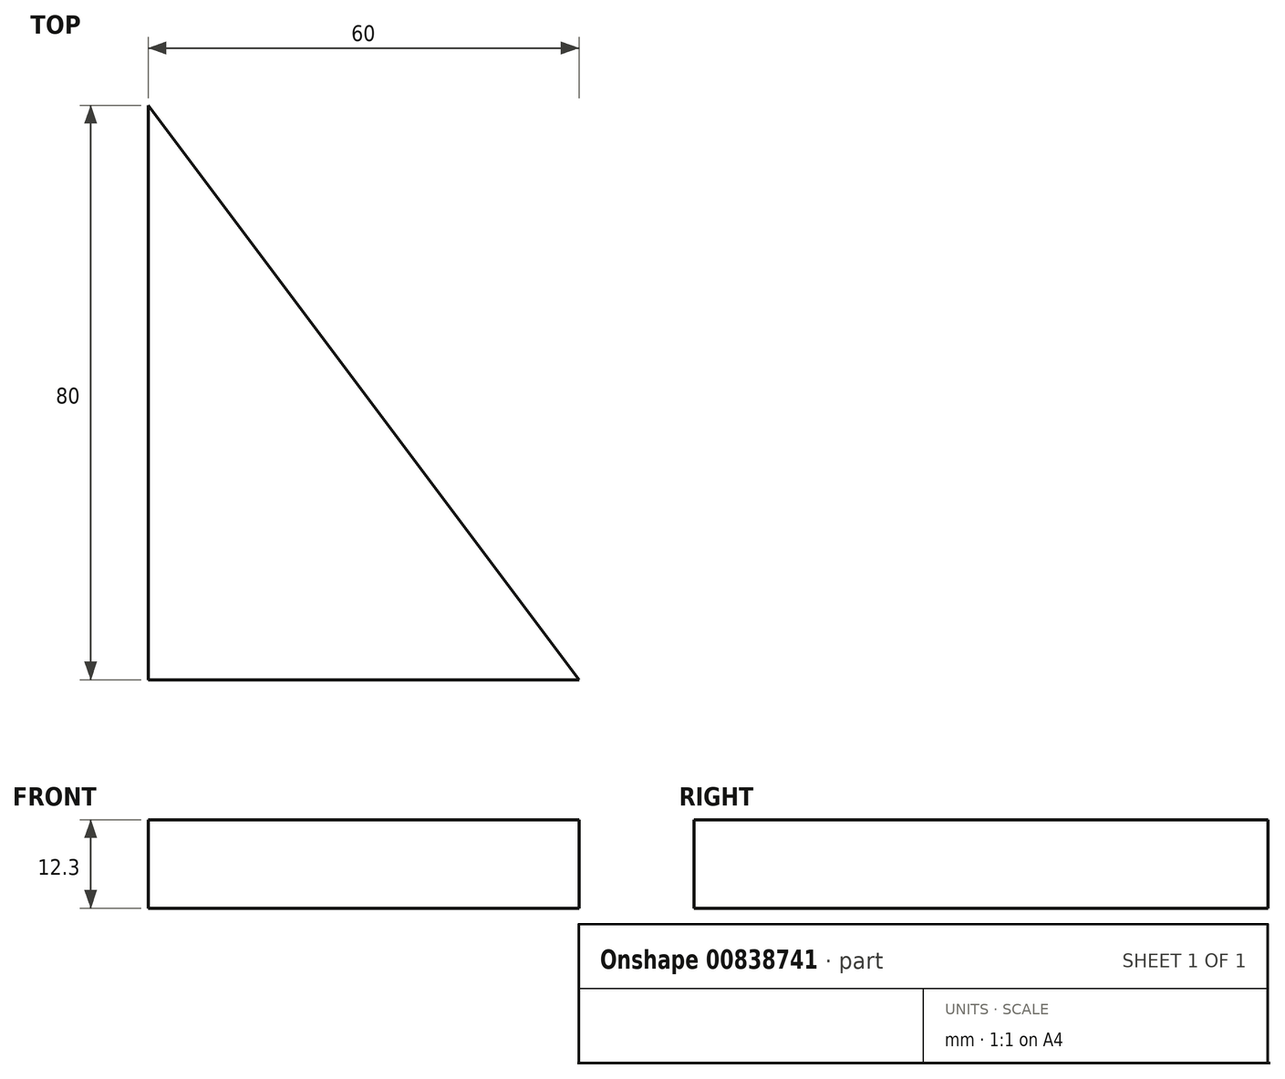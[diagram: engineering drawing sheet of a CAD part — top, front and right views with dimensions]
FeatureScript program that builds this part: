
annotation { "Feature Type Name" : "Feature", "Feature Type Description" : "" }
export const myFeature = defineFeature(function(context is Context, id is Id, definition is map)
    precondition{}
    {
        {
            var Q0;
            Q0=qCreatedBy(makeId("Top.planeOp"),FACE);
            var sketch = newSketch(context, id + "F0", { "sketchPlane" : qUnion([Q0])});
            skLineSegment(sketch, "E0", {"start": v(0, 0) * mm, "end": v(0, 80) * mm});
            skLineSegment(sketch, "E1", {"start": v(0, 80) * mm, "end": v(60, 0) * mm});
            skLineSegment(sketch, "E2", {"start": v(60, 0) * mm, "end": v(0, 0) * mm});
            skSolve(sketch);
        }
        {
            var Q0;
            Q0=makeQuery(id+"F0.imprint","IMPRINT",FACE,{"disambiguationData":[TD([[makeQuery(id+"F0.imprint","IMPRINT",EDGE,{"derivedFrom":sQuery(id+"F0.wireOp",EDGE,"E0")}),-1.0]])]});
            extrude(context, id + "F1", {"entities" : qUnion([Q0]), "depth" : 12.3 * mm, "offsetDistance" : 25 * mm});
        }
    });
